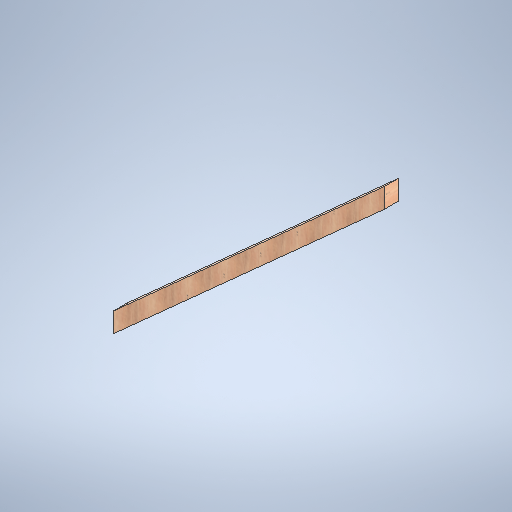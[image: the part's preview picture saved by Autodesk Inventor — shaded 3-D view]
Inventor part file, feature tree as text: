
AUTODESK INVENTOR PART (.ipt)
format: ipt  version: 2025 (Build 290162000, 162)  size: 274,944 bytes
history: native  units: in
note: dims shown in document units (in); Inventor stores cm internally (conversion verified against a paired STEP export)
features: extrude x1, sketch x1
ambient origin geometry x8: Origin, YZ Plane, XZ Plane, XY Plane, X Axis, Y Axis, Z Axis, Center Point
bodies: Solid1 (feature_tree)
feature tree (2):
  extrude  "Extrusion1"  Depth=4.0in TaperAngle=0.0deg
  sketch  "Sketch1"  dims[d5=4.0in d6=90.0deg d7=90.0deg d9=4.0in d10=0.0in]
